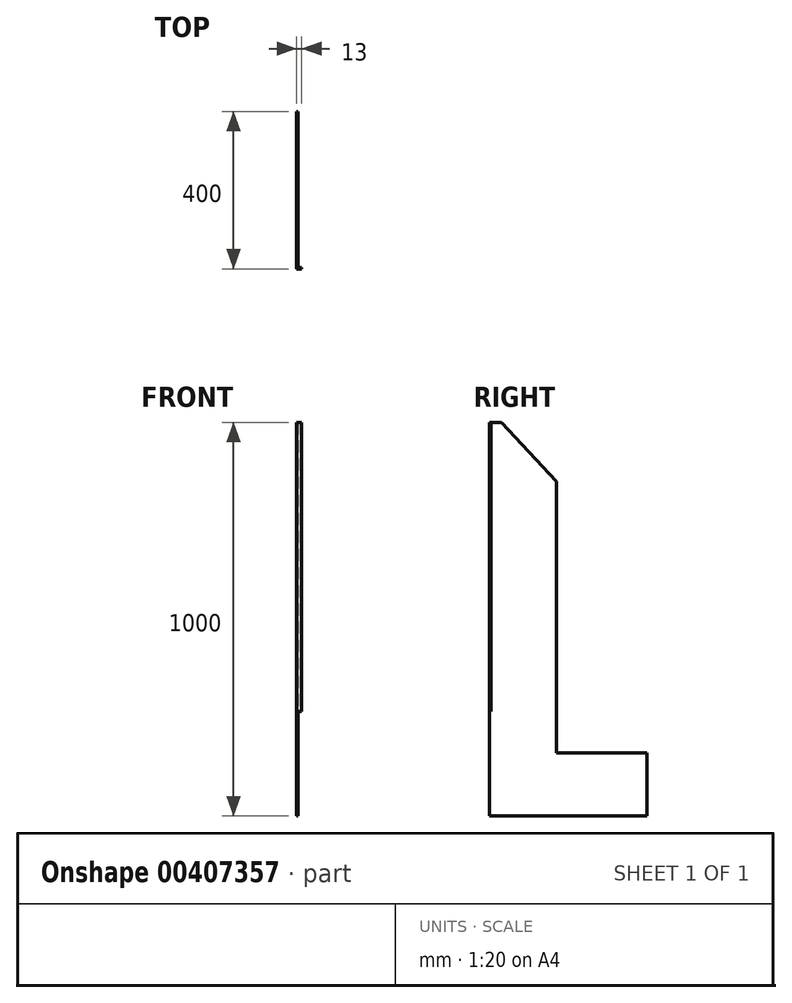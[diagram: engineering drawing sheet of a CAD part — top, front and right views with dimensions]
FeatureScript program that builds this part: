
annotation { "Feature Type Name" : "Feature", "Feature Type Description" : "" }
export const myFeature = defineFeature(function(context is Context, id is Id, definition is map)
    precondition{}
    {
        {
            var Q0;
            Q0=qCreatedBy(makeId("Right.planeOp"),FACE);
            var sketch = newSketch(context, id + "F0", { "sketchPlane" : qUnion([Q0])});
            skLineSegment(sketch, "E0", {"start": v(0, 0) * mm, "end": v(0, 160) * mm});
            skLineSegment(sketch, "E1", {"start": v(0, 160) * mm, "end": v(-230, 160) * mm});
            skLineSegment(sketch, "E2", {"start": v(-230, 160) * mm, "end": v(-230, 850) * mm});
            skLineSegment(sketch, "E3", {"start": v(-400, 1000) * mm, "end": v(-400, 0) * mm});
            skLineSegment(sketch, "E4", {"start": v(-400, 0) * mm, "end": v(0, 0) * mm});
            skLineSegment(sketch, "E5", {"start": v(-230, 850) * mm, "end": v(-370, 1000) * mm});
            skLineSegment(sketch, "E6", {"start": v(-370, 1000) * mm, "end": v(-400, 1000) * mm});
            skSolve(sketch);
        }
        {
            var Q0;
            Q0=makeQuery(id+"F0.imprint","IMPRINT",FACE,{"disambiguationData":[TD([[makeQuery(id+"F0.imprint","IMPRINT",EDGE,{"derivedFrom":sQuery(id+"F0.wireOp",EDGE,"E0")}),1.0]])]});
            extrude(context, id + "F1", {"entities" : qUnion([Q0]), "depth" : 3 * mm});
        }
        {
            var Q0;
            Q0=makeQuery(id+"F1.opExtrude","CAP_FACE",FACE,{"disambiguationData":[OSD([sQuery(id+"F0.wireOp",EDGE,"E0"),sQuery(id+"F0.wireOp",EDGE,"E1"),sQuery(id+"F0.wireOp",EDGE,"E2"),sQuery(id+"F0.wireOp",EDGE,"E3"),sQuery(id+"F0.wireOp",EDGE,"E4"),sQuery(id+"F0.wireOp",EDGE,"E5"),sQuery(id+"F0.wireOp",EDGE,"E6")])],"isStart":false});
            var sketch = newSketch(context, id + "F2", { "sketchPlane" : qUnion([Q0])});
            skLineSegment(sketch, "E7", {"start": v(-397, 1000) * mm, "end": v(-397, 266) * mm});
            skLineSegment(sketch, "E8", {"start": v(-397, 266) * mm, "end": v(-400, 266) * mm});
            skSolve(sketch);
        }
        {
            var Q0;
            {var subQ0=sQuery(id+"F2.wireOp",EDGE,"E7");Q0=makeQuery(id+"F2.imprint","IMPRINT",FACE,{"disambiguationData":[TD([[makeQuery(id+"F2.imprint","IMPRINT",EDGE,{"derivedFrom":subQ0}),-1.0]])]});}
            extrude(context, id + "F3", {"entities" : qUnion([Q0]), "operationType" : NewBodyOperationType.ADD, "depth" : 10 * mm});
        }
    });
